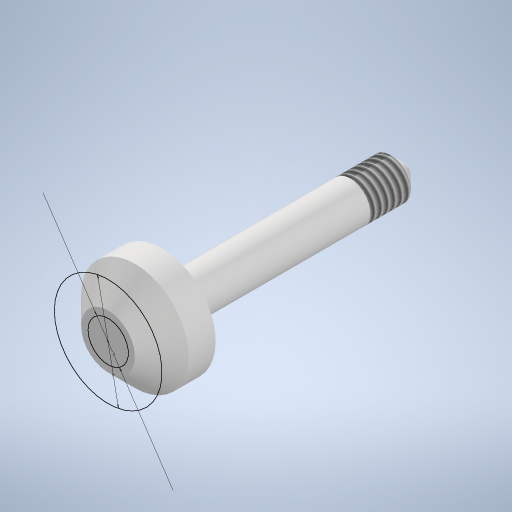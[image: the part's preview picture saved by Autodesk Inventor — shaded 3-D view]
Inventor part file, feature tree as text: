
AUTODESK INVENTOR PART (.ipt)
format: ipt  version: 2024 (Build 280153000, 153)  size: 264,192 bytes
history: native  units: mm
features: extrude x2, chamfer x2, sketch x1, thread x1
ambient origin geometry x8: Origin, YZ Plane, XZ Plane, XY Plane, X Axis, Y Axis, Z Axis, Center Point
bodies: Solid1 (feature_tree)
feature tree (6):
  sketch  "Sketch1"  dims[d0=3.0mm d1=8.0mm d2=22.0mm d3=0.0mm d4=4.0mm d5=0.0mm d6=2.0mm d7=2.0mm d8=45.0deg d9=4.0mm d10=0.0mm d11=1.0mm d12=2.0mm d13=45.0deg]
  extrude  "Extrusion1"  Depth=1.0mm
  extrude  "Extrusion2"  Depth=22.0mm TaperAngle=0.0deg
  chamfer  "Chamfer1"  Distance=4.0mm
  thread  "Thread1"  [1 undecoded]
  chamfer  "Chamfer2"  Distance=4.0mm
note: 1 required parameter value undecoded (feature->parameter linkage not recoverable at this tier; creation-order binding heuristic only, values carry confidence <= 0.55)
